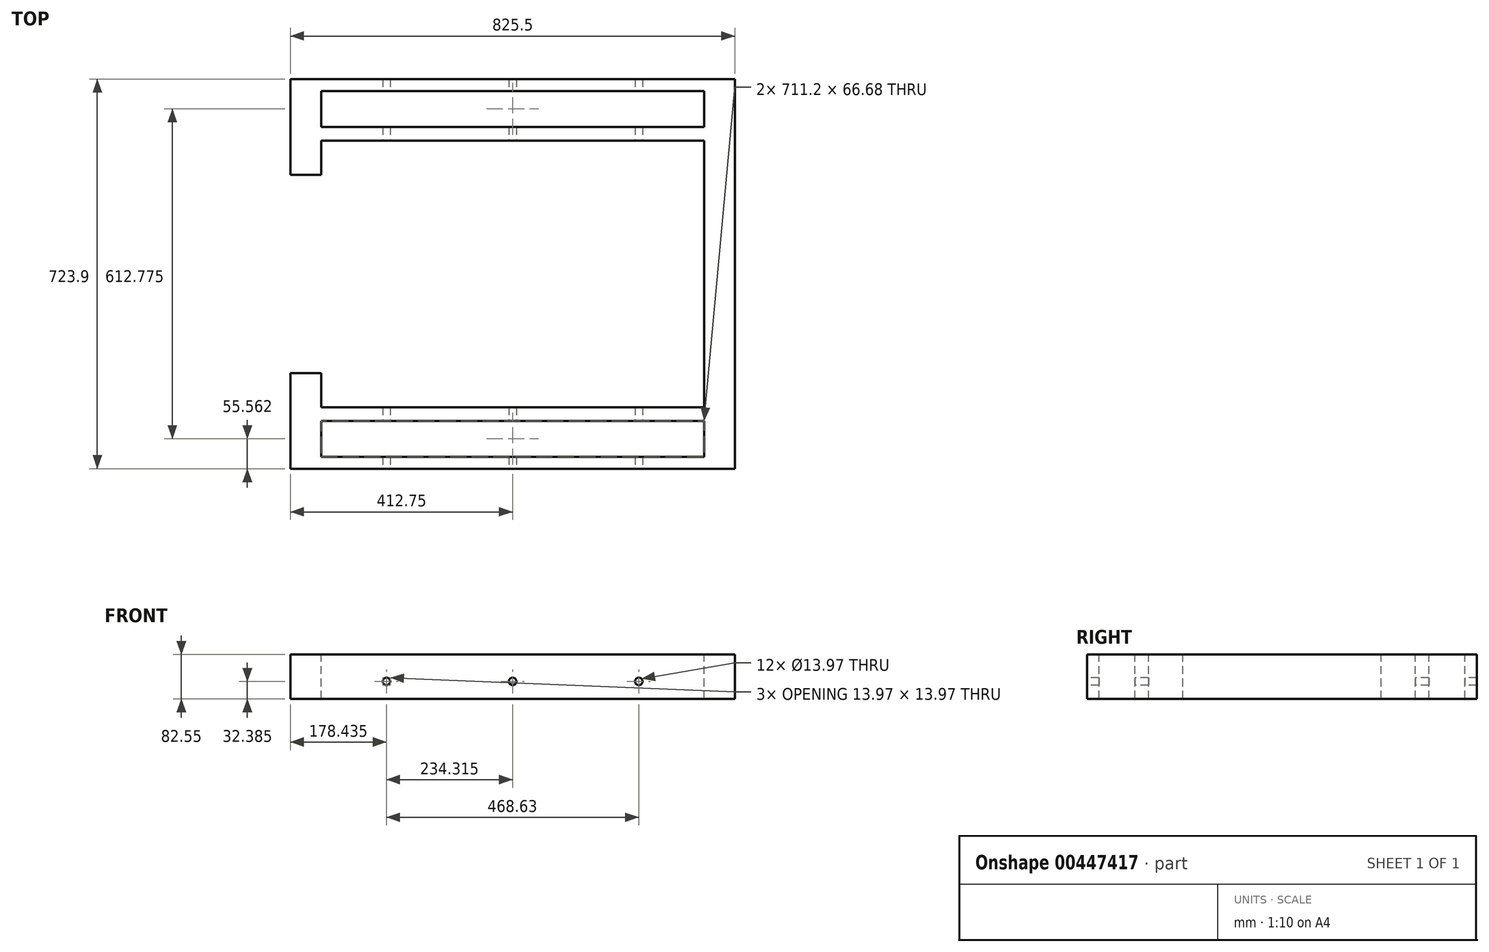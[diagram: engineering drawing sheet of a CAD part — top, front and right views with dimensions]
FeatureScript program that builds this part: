
annotation { "Feature Type Name" : "Feature", "Feature Type Description" : "" }
export const myFeature = defineFeature(function(context is Context, id is Id, definition is map)
    precondition{}
    {
        {
            var Q0;
            Q0=qCreatedBy(makeId("Top.planeOp"),FACE);
            var sketch = newSketch(context, id + "F0", { "sketchPlane" : qUnion([Q0])});
            skLineSegment(sketch, "E0.bottom", {"start": v(412.75, 361.95) * mm, "end": v(-412.75, 361.95) * mm});
            skLineSegment(sketch, "E0.top", {"start": v(412.75, -361.95) * mm, "end": v(-412.75, -361.95) * mm});
            skLineSegment(sketch, "E0.left", {"start": v(412.75, 361.95) * mm, "end": v(412.75, -361.95) * mm});
            skLineSegment(sketch, "E0.right", {"start": v(-412.75, 361.95) * mm, "end": v(-412.75, -361.95) * mm});
            skPoint(sketch, "E0.middle", {"position": v(0, 0) * mm});
            skSolve(sketch);
        }
        {
            var Q0;
            Q0=makeQuery(id+"F0.imprint","IMPRINT",FACE,{"disambiguationData":[TD([[makeQuery(id+"F0.imprint","IMPRINT",EDGE,{"derivedFrom":sQuery(id+"F0.wireOp",EDGE,"E0.bottom")}),1.0]])]});
            extrude(context, id + "F1", {"entities" : qUnion([Q0]), "depth" : 82.55 * mm});
        }
        {
            var Q0;
            Q0=makeQuery(id+"F1.opExtrude","CAP_FACE",FACE,{"disambiguationData":[OSD([sQuery(id+"F0.wireOp",EDGE,"E0.bottom"),sQuery(id+"F0.wireOp",EDGE,"E0.top"),sQuery(id+"F0.wireOp",EDGE,"E0.left"),sQuery(id+"F0.wireOp",EDGE,"E0.right")])],"isStart":false});
            var sketch = newSketch(context, id + "F2", { "sketchPlane" : qUnion([Q0])});
            skLineSegment(sketch, "E1.bottom", {"start": v(355.6, 247.65) * mm, "end": v(-355.6, 247.65) * mm});
            skLineSegment(sketch, "E1.top", {"start": v(355.6, -247.65) * mm, "end": v(-355.6, -247.65) * mm});
            skLineSegment(sketch, "E1.left", {"start": v(355.6, 247.65) * mm, "end": v(355.6, -247.65) * mm});
            skLineSegment(sketch, "E1.right", {"start": v(-355.6, 247.65) * mm, "end": v(-355.6, -247.65) * mm});
            skPoint(sketch, "E1.middle", {"position": v(0, 0) * mm});
            skSolve(sketch);
        }
        {
            var Q0;
            Q0 = qSketchRegion(id + "F2", true);
            extrude(context, id + "F3", {"entities" : qUnion([Q0]), "operationType" : NewBodyOperationType.REMOVE, "oppositeDirection" : true, "depth" : 82.55 * mm});
        }
        {
            var Q0;
            Q0=makeQuery(id+"F1.opExtrude","CAP_FACE",FACE,{"disambiguationData":[OSD([sQuery(id+"F0.wireOp",EDGE,"E0.bottom"),sQuery(id+"F0.wireOp",EDGE,"E0.top"),sQuery(id+"F0.wireOp",EDGE,"E0.left"),sQuery(id+"F0.wireOp",EDGE,"E0.right")])],"isStart":false});
            var sketch = newSketch(context, id + "F4", { "sketchPlane" : qUnion([Q0])});
            skLineSegment(sketch, "E2.bottom", {"start": v(355.6, 339.73) * mm, "end": v(-355.6, 339.73) * mm});
            skLineSegment(sketch, "E2.top", {"start": v(355.6, 273.05) * mm, "end": v(-355.6, 273.05) * mm});
            skLineSegment(sketch, "E2.left", {"start": v(355.6, 339.73) * mm, "end": v(355.6, 273.05) * mm});
            skLineSegment(sketch, "E2.right", {"start": v(-355.6, 339.73) * mm, "end": v(-355.6, 273.05) * mm});
            skPoint(sketch, "E2.middle", {"position": v(0, 306.39) * mm});
            skSolve(sketch);
        }
        {
            var Q0;
            Q0=makeQuery(id+"F4.imprint","IMPRINT",FACE,{"disambiguationData":[TD([[makeQuery(id+"F4.imprint","IMPRINT",EDGE,{"derivedFrom":sQuery(id+"F4.wireOp",EDGE,"E2.bottom")}),1.0]])]});
            extrude(context, id + "F5", {"entities" : qUnion([Q0]), "operationType" : NewBodyOperationType.REMOVE, "oppositeDirection" : true, "depth" : 82.55 * mm});
        }
        {
            var Q0;
            Q0=makeQuery(id+"F1.opExtrude","CAP_FACE",FACE,{"disambiguationData":[OSD([sQuery(id+"F0.wireOp",EDGE,"E0.bottom"),sQuery(id+"F0.wireOp",EDGE,"E0.top"),sQuery(id+"F0.wireOp",EDGE,"E0.left"),sQuery(id+"F0.wireOp",EDGE,"E0.right")])],"isStart":false});
            var sketch = newSketch(context, id + "F6", { "sketchPlane" : qUnion([Q0])});
            skLineSegment(sketch, "E3.bottom", {"start": v(355.6, -273.05) * mm, "end": v(-355.6, -273.05) * mm});
            skLineSegment(sketch, "E3.top", {"start": v(355.6, -339.73) * mm, "end": v(-355.6, -339.73) * mm});
            skLineSegment(sketch, "E3.left", {"start": v(355.6, -273.05) * mm, "end": v(355.6, -339.73) * mm});
            skLineSegment(sketch, "E3.right", {"start": v(-355.6, -273.05) * mm, "end": v(-355.6, -339.73) * mm});
            skPoint(sketch, "E3.middle", {"position": v(0, -306.39) * mm});
            skSolve(sketch);
        }
        {
            var Q0;
            Q0 = qSketchRegion(id + "F6", true);
            extrude(context, id + "F7", {"entities" : qUnion([Q0]), "operationType" : NewBodyOperationType.REMOVE, "oppositeDirection" : true, "depth" : 82.55 * mm});
        }
        {
            var Q0;
            Q0=makeQuery(id+"F1.opExtrude","SWEPT_FACE",FACE,{"disambiguationData":[OSD([sQuery(id+"F0.wireOp",EDGE,"E0.right")])]});
            var sketch = newSketch(context, id + "F8", { "sketchPlane" : qUnion([Q0])});
            skLineSegment(sketch, "E4.bottom", {"start": v(184.15, 0) * mm, "end": v(-184.15, 0) * mm});
            skLineSegment(sketch, "E4.top", {"start": v(184.15, 82.55) * mm, "end": v(-184.15, 82.55) * mm});
            skLineSegment(sketch, "E4.left", {"start": v(184.15, 0) * mm, "end": v(184.15, 82.55) * mm});
            skLineSegment(sketch, "E4.right", {"start": v(-184.15, 0) * mm, "end": v(-184.15, 82.55) * mm});
            skPoint(sketch, "E4.middle", {"position": v(0, 41.28) * mm});
            skPoint(sketch, "E4.middle.positionSnap0", {"position": v(0, 0) * mm});
            skPoint(sketch, "E4.centerSnap0", {"position": v(0, 0) * mm});
            skSolve(sketch);
        }
        {
            var Q0;
            Q0 = qSketchRegion(id + "F8", true);
            extrude(context, id + "F9", {"entities" : qUnion([Q0]), "operationType" : NewBodyOperationType.REMOVE, "oppositeDirection" : true, "depth" : 57.15 * mm});
        }
        {
            var Q0;
            Q0=makeQuery(id+"F1.opExtrude","SWEPT_FACE",FACE,{"disambiguationData":[OSD([sQuery(id+"F0.wireOp",EDGE,"E0.top")])]});
            var sketch = newSketch(context, id + "F10", { "sketchPlane" : qUnion([Q0])});
            skCircle(sketch, "E5", {"center": v(0, 32.39) * mm, "radius": 6.99 * mm});
            skCircle(sketch, "E6", {"center": v(234.32, 32.39) * mm, "radius": 6.99 * mm});
            skCircle(sketch, "E7", {"center": v(-234.31, 32.39) * mm, "radius": 6.99 * mm});
            skSolve(sketch);
        }
        {
            var Q0;
            Q0 = qSketchRegion(id + "F10", true);
            extrude(context, id + "F11", {"entities" : qUnion([Q0]), "operationType" : NewBodyOperationType.REMOVE, "oppositeDirection" : true, "depth" : 762 * mm});
        }
    });
